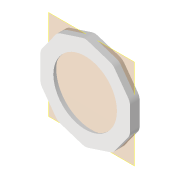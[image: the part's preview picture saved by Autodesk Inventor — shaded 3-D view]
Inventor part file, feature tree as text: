
AUTODESK INVENTOR PART (.ipt)
format: ipt  version: 2022 (Build 260153000, 153)  size: 217,088 bytes
history: native  units: mm
features: reference x5, other x4, extrude x3, sketch x3, projected_geometry x2, plane x1
ambient origin geometry x8: Origin, YZ Plane, XZ Plane, XY Plane, X Axis, Y Axis, Z Axis, Center Point
bodies: Volumenkörper1 (feature_tree)
feature tree (18):
  plane  "Arbeitsebene1"
  extrude  "Extrusion1"  Depth=1.0mm
  extrude  "Extrusion2"  Depth=3.0mm
  extrude  "Extrusion3"  Depth=2.3mm
  sketch  "Skizze1"  dims[d0=5.0mm d1=1.0mm]
  reference  "Referenz1"
  reference  "Referenz2"
  reference  "Referenz3"
  sketch  "Skizze2"  dims[d2=4.5mm d3=0.0mm d4=3.0mm]
  projected_geometry  "Projizierte Kontur1"
  sketch  "Skizze3"  dims[d5=1.0mm d6=0.0mm d7=2.3mm d8=3.0mm d9=0.0mm]
  reference  "Referenz4"
  reference  "Referenz5"
  projected_geometry  "Projizierte Kontur2"
  other  "Anglerfish_bonne_mamman_m12large_v0.iam"
  other  "00_bonne_maman_jar:1"
  other  "Anglerfish_Jar_Adapterplate_v1:1"
  other  "Anglerfish_Lightplate_Tosslink:1"
